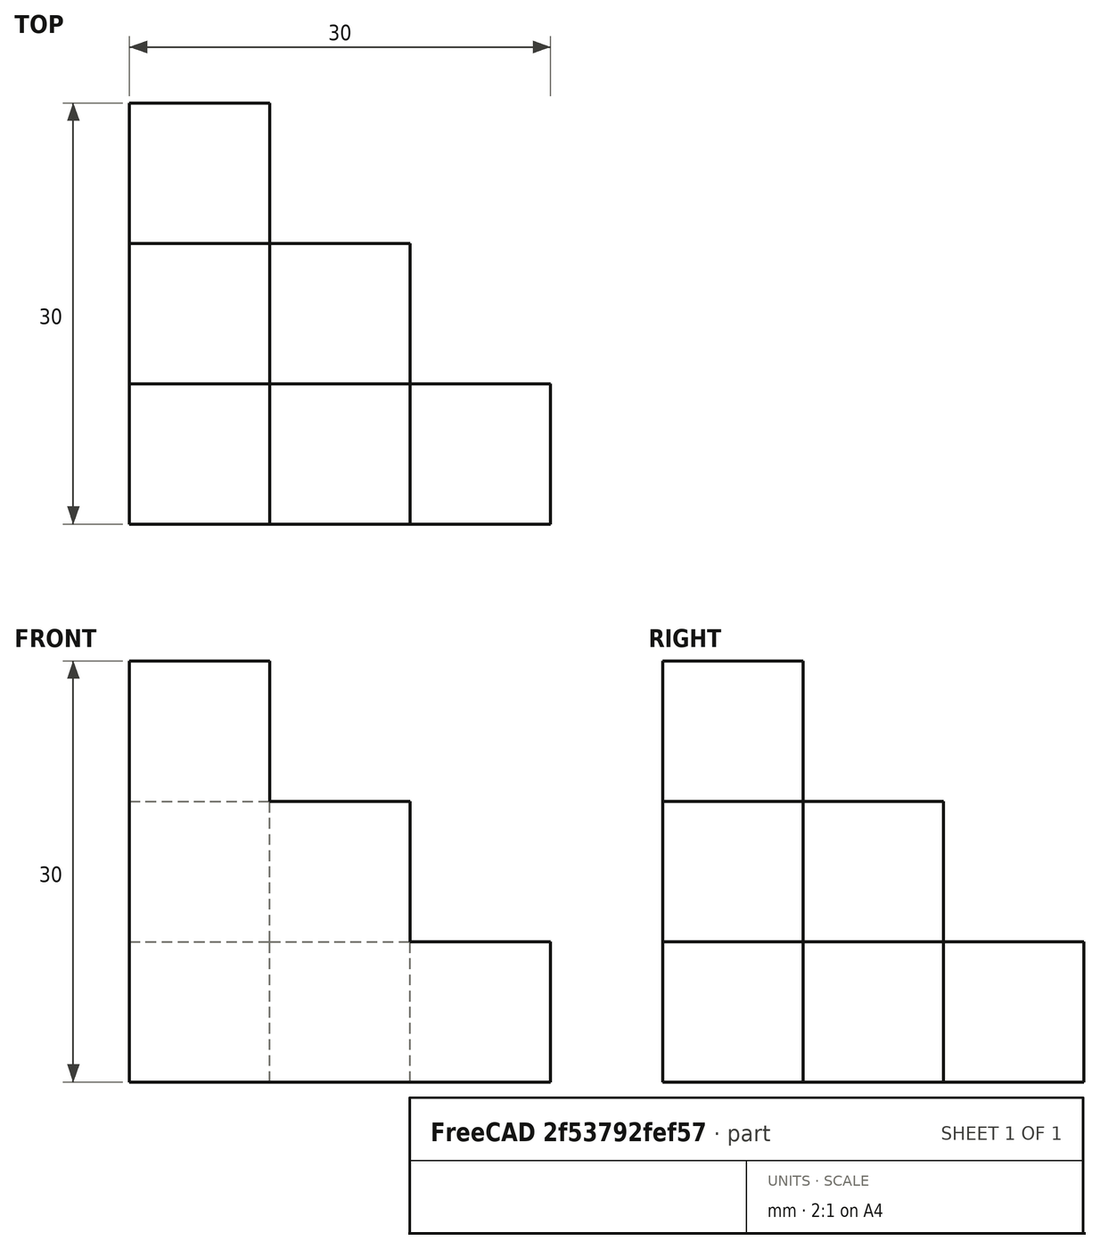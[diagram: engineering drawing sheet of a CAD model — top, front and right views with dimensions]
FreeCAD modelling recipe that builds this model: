
FCSTD DOCUMENT  (FreeCAD 0.16R6706 (Git))
Label: Portalapices
License: All rights reserved
LicenseURL: http://en.wikipedia.org/wiki/All_rights_reserved
objects: Part::Box×10, Part::MultiFuse×1
note: 11 computed .brp shape members not serialized (recipe doc carries the construction recipe); baked Part::Feature solids carry a one-line shape summary decoded from their .brp

FEATURE [Part::Box] Box  label=" cubo 000"
  Height = 10
  Length = 10
  Width = 10
FEATURE [Part::Box] Box001  label="Cubo 100"
  Height = 10
  Length = 10
  Placement = pos=(10,0,0) rot=(0,0,1;0rad)
  Width = 10
FEATURE [Part::Box] Box002  label="Cubo 200"
  Height = 10
  Length = 10
  Placement = pos=(20,0,0) rot=(0,0,1;0rad)
  Width = 10
FEATURE [Part::Box] Box003  label="Cubo 010"
  Height = 10
  Length = 10
  Placement = pos=(0,10,0) rot=(0,0,1;0rad)
  Width = 10
FEATURE [Part::Box] Box004  label="Cubo004"
  Height = 10
  Length = 10
  Placement = pos=(0,20,0) rot=(0,0,1;0rad)
  Width = 10
FEATURE [Part::Box] Box005  label="Cubo005"
  Height = 10
  Length = 10
  Placement = pos=(10,10,0) rot=(0,0,1;0rad)
  Width = 10
FEATURE [Part::Box] Box006  label="Cubo006"
  Height = 10
  Length = 10
  Placement = pos=(0,0,10) rot=(0,0,1;0rad)
  Width = 10
FEATURE [Part::Box] Box007  label="Cubo007"
  Height = 10
  Length = 10
  Placement = pos=(0,0,20) rot=(0,0,1;0rad)
  Width = 10
FEATURE [Part::Box] Box008  label="Cubo008"
  Height = 10
  Length = 10
  Placement = pos=(0,10,10) rot=(0,0,1;0rad)
  Width = 10
FEATURE [Part::Box] Box009  label="Cubo009"
  Height = 10
  Length = 10
  Placement = pos=(10,0,10) rot=(0,0,1;0rad)
  Width = 10
FEATURE [Part::MultiFuse] Fusion
  Shapes = -> [Box003,Box002,Box004,Box005,Box006,Box007,Box008,Box009,Box,Box001]
